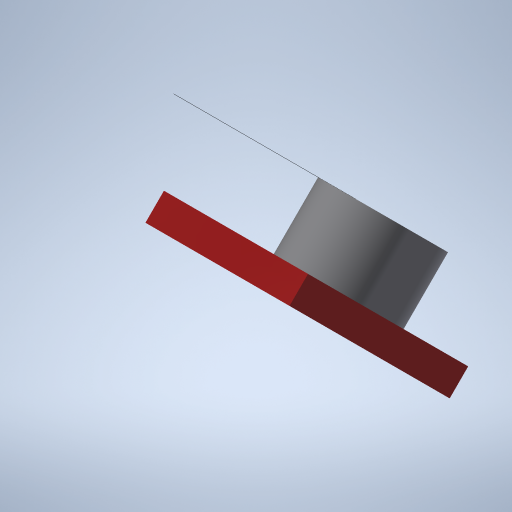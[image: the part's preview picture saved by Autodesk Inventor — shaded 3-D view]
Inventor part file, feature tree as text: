
AUTODESK INVENTOR PART (.ipt)
format: ipt  version: 2024.2 (Build 282272000, 272)  size: 279,552 bytes
history: native  units: in
note: dims shown in document units (in); Inventor stores cm internally (conversion verified against a paired STEP export)
features: other x3, thread x2, imported_body x1
ambient origin geometry x8: Origin, YZ Plane, XZ Plane, XY Plane, X Axis, Y Axis, Z Axis, Center Point
bodies: Body1 (feature_tree)
feature tree (6):
  other  "product-name"
  other  "Annotations"
  other  "product-name1"
  thread  "Thread1"  [1 undecoded]
  imported_body  "Base1"
  thread  "Thread Note 1"  [1 undecoded]
note: 2 required parameter values undecoded (feature->parameter linkage not recoverable at this tier; creation-order binding heuristic only, values carry confidence <= 0.55)
